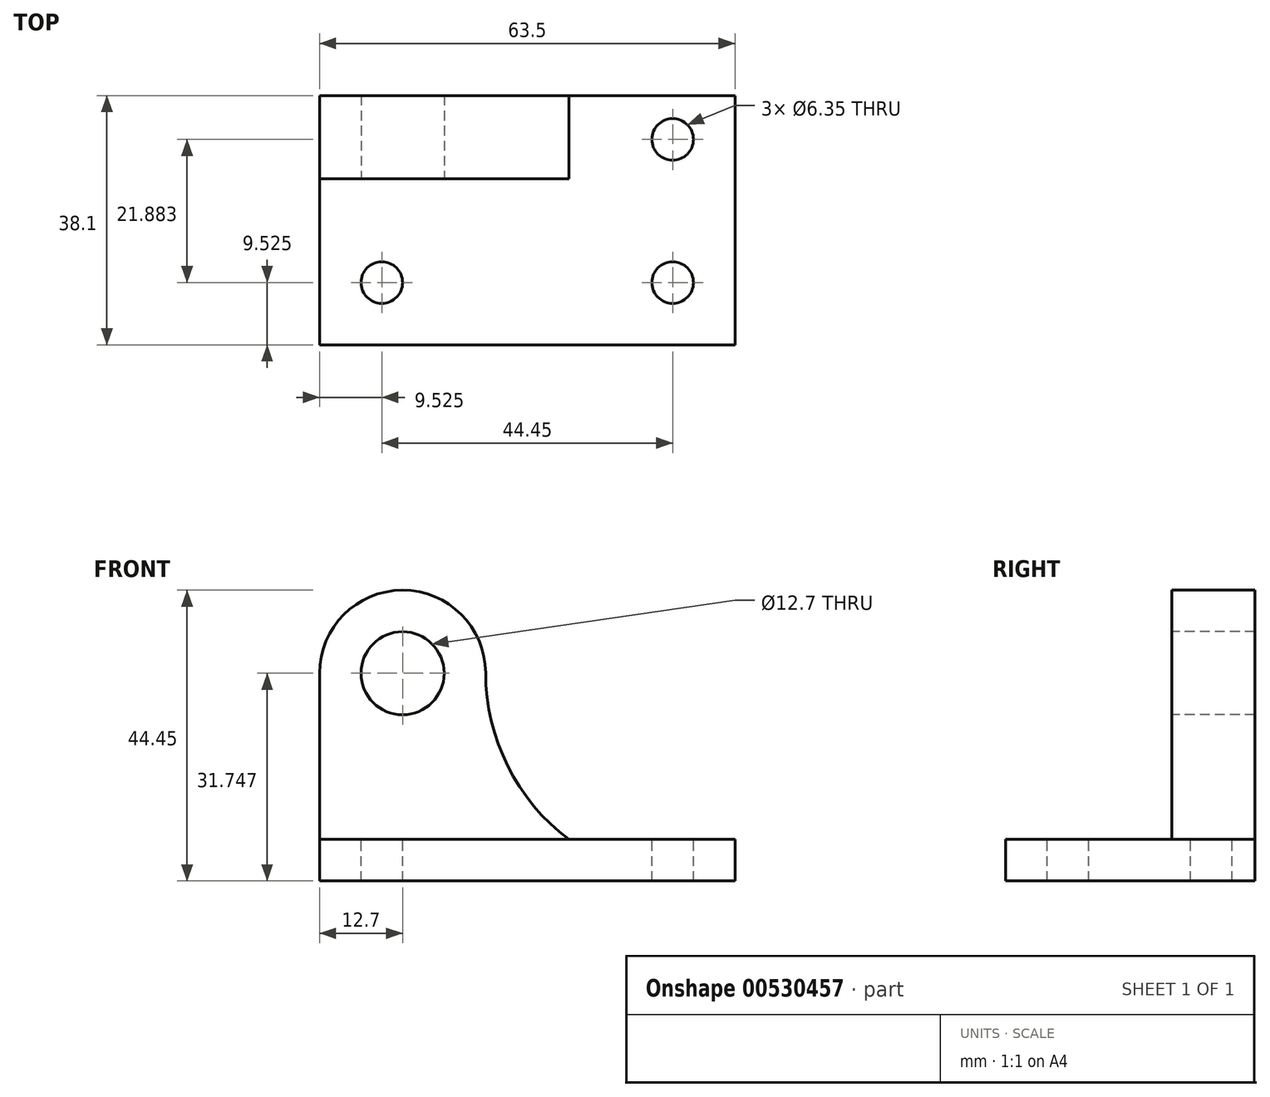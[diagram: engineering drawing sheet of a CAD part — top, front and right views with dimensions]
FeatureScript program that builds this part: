
annotation { "Feature Type Name" : "Feature", "Feature Type Description" : "" }
export const myFeature = defineFeature(function(context is Context, id is Id, definition is map)
    precondition{}
    {
        {
            var Q0;
            Q0=qCreatedBy(makeId("Front.planeOp"),FACE);
            var sketch = newSketch(context, id + "F0", { "sketchPlane" : qUnion([Q0])});
            skLineSegment(sketch, "E0", {"start": v(-54.83, 53.99) * mm, "end": v(-54.83, 9.54) * mm});
            skLineSegment(sketch, "E1", {"start": v(-54.83, 9.54) * mm, "end": v(8.67, 9.54) * mm});
            skLineSegment(sketch, "E2", {"start": v(8.67, 9.54) * mm, "end": v(8.67, 15.89) * mm});
            skLineSegment(sketch, "E3", {"start": v(8.67, 15.89) * mm, "end": v(-16.73, 15.89) * mm});
            skLineSegment(sketch, "E4", {"start": v(-16.73, 15.89) * mm, "end": v(-16.73, 53.99) * mm});
            skLineSegment(sketch, "E5", {"start": v(-16.73, 53.99) * mm, "end": v(-54.83, 53.99) * mm});
            skArc(sketch, "E6", {"start": v(-29.43, 41.32) * mm, "mid": v(-42.15, 53.99) * mm, "end": v(-54.83, 41.29) * mm});
            skArc(sketch, "E7", {"start": v(-29.43, 41.32) * mm, "mid": v(-26.06, 27.12) * mm, "end": v(-16.73, 15.89) * mm});
            skSolve(sketch);
        }
        {
            var Q0;
            {var subQ0=sQuery(id+"F0.wireOp",EDGE,"E1");Q0=makeQuery(id+"F0.imprint","IMPRINT",FACE,{"disambiguationData":[TD([[makeQuery(id+"F0.imprint","IMPRINT",EDGE,{"derivedFrom":subQ0}),1.0]])]});}
            extrude(context, id + "F1", {"entities" : qUnion([Q0]), "depth" : 38.1 * mm, "offsetDistance" : 25.4 * mm});
        }
        {
            var Q0;
            Q0=makeQuery(id+"F1.opExtrude","CAP_FACE",FACE,{"disambiguationData":[OSD([sQuery(id+"F0.wireOp",EDGE,"E0"),sQuery(id+"F0.wireOp",EDGE,"E1"),sQuery(id+"F0.wireOp",EDGE,"E2"),sQuery(id+"F0.wireOp",EDGE,"E3"),sQuery(id+"F0.wireOp",EDGE,"E6"),sQuery(id+"F0.wireOp",EDGE,"E7")])],"isStart":false});
            var sketch = newSketch(context, id + "F2", { "sketchPlane" : qUnion([Q0])});
            skLineSegment(sketch, "E8", {"start": v(-16.73, 15.89) * mm, "end": v(-54.83, 15.89) * mm});
            skSolve(sketch);
        }
        {
            var Q0;
            Q0 = qSketchRegion(id + "F2", true);
            var Q1;
            {var subQ0=sQuery(id+"F2.wireOp",EDGE,"E8");Q1=makeQuery(id+"F2.imprint","IMPRINT",FACE,{"disambiguationData":[TD([[makeQuery(id+"F2.imprint","IMPRINT",EDGE,{"derivedFrom":subQ0}),-1.0]])]});}
            extrude(context, id + "F3", {"entities" : qUnion([Q0, Q1]), "operationType" : NewBodyOperationType.REMOVE, "oppositeDirection" : true, "depth" : 25.4 * mm, "offsetDistance" : 25.4 * mm});
        }
        {
            var Q0;
            Q0=makeQuery(id+"F3.boolean.opBoolean","COPY",FACE,{"derivedFrom":makeQuery(id+"F3.opExtrude","CAP_FACE",FACE,{"disambiguationData":[OSD([sQuery(id+"F0.wireOp",EDGE,"E0"),sQuery(id+"F0.wireOp",EDGE,"E6"),sQuery(id+"F0.wireOp",EDGE,"E7"),sQuery(id+"F2.wireOp",EDGE,"E8")])],"isStart":false})});
            var sketch = newSketch(context, id + "F4", { "sketchPlane" : qUnion([Q0])});
            skCircle(sketch, "E9", {"center": v(-42.13, 41.29) * mm, "radius": 6.35 * mm});
            skSolve(sketch);
        }
        {
            var Q0;
            Q0 = qSketchRegion(id + "F4", true);
            extrude(context, id + "F5", {"entities" : qUnion([Q0]), "operationType" : NewBodyOperationType.REMOVE, "endBound" : BoundingType.THROUGH_ALL, "oppositeDirection" : true, "depth" : 25.4 * mm, "offsetDistance" : 25.4 * mm});
        }
        {
            var Q0;
            Q0=makeQuery(id+"F3.boolean.opBoolean","MERGE",FACE,{"derivedFrom":[makeQuery(id+"F1.opExtrude","SWEPT_FACE",FACE,{"disambiguationData":[OSD([sQuery(id+"F0.wireOp",EDGE,"E3")])]}),makeQuery(id+"F3.opExtrude","SWEPT_FACE",FACE,{"disambiguationData":[OSD([sQuery(id+"F2.wireOp",EDGE,"E8")])]})]});
            var sketch = newSketch(context, id + "F6", { "sketchPlane" : qUnion([Q0])});
            skCircle(sketch, "E10", {"center": v(-0.85, -6.7) * mm, "radius": 3.18 * mm});
            skCircle(sketch, "E11", {"center": v(-0.85, -28.58) * mm, "radius": 3.18 * mm});
            skCircle(sketch, "E12", {"center": v(-45.3, -28.58) * mm, "radius": 3.18 * mm});
            skSolve(sketch);
        }
        {
            var Q0;
            Q0 = qSketchRegion(id + "F6", true);
            extrude(context, id + "F7", {"entities" : qUnion([Q0]), "operationType" : NewBodyOperationType.REMOVE, "endBound" : BoundingType.THROUGH_ALL, "oppositeDirection" : true, "depth" : 25.4 * mm, "offsetDistance" : 25.4 * mm});
        }
    });
